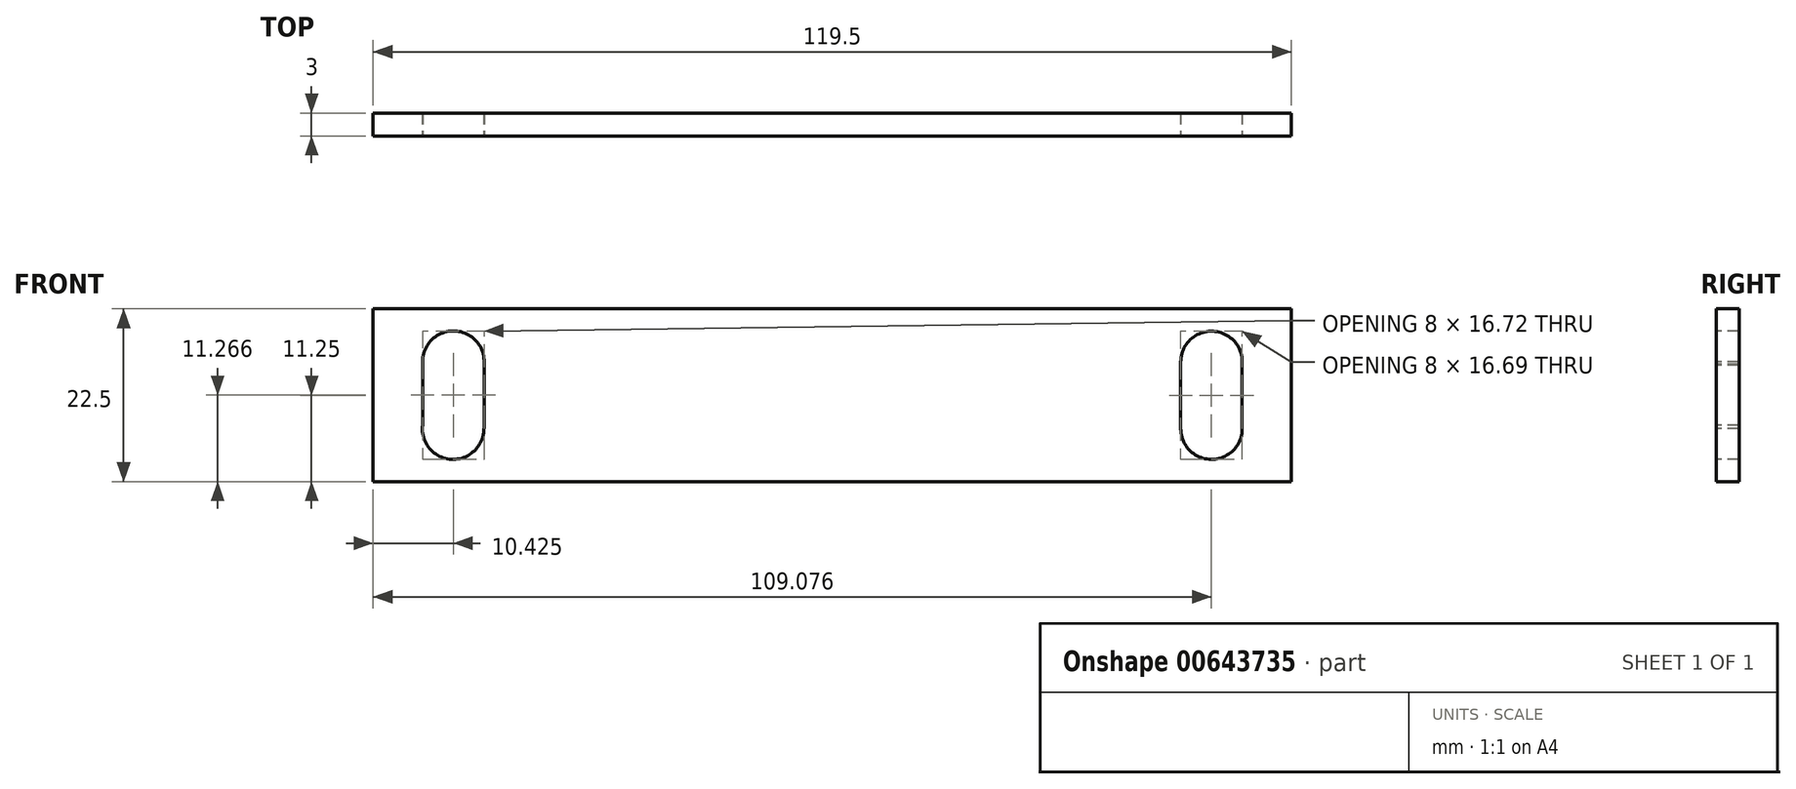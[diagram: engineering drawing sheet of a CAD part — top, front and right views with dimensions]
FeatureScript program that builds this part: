
annotation { "Feature Type Name" : "Feature", "Feature Type Description" : "" }
export const myFeature = defineFeature(function(context is Context, id is Id, definition is map)
    precondition{}
    {
        {
            var Q0;
            Q0=qCreatedBy(makeId("Front.planeOp"),FACE);
            var sketch = newSketch(context, id + "F0", { "sketchPlane" : qUnion([Q0])});
            skLineSegment(sketch, "E0.bottom", {"start": v(59.75, 11.25) * mm, "end": v(-59.75, 11.25) * mm});
            skLineSegment(sketch, "E0.top", {"start": v(59.75, -11.25) * mm, "end": v(-59.75, -11.25) * mm});
            skLineSegment(sketch, "E0.left", {"start": v(59.75, 11.25) * mm, "end": v(59.75, -11.25) * mm});
            skLineSegment(sketch, "E0.right", {"start": v(-59.75, 11.25) * mm, "end": v(-59.75, -11.25) * mm});
            skPoint(sketch, "E0.middle", {"position": v(0, 0) * mm});
            skSolve(sketch);
        }
        {
            var Q0;
            Q0=makeQuery(id+"F0.imprint","IMPRINT",FACE,{"disambiguationData":[TD([[makeQuery(id+"F0.imprint","IMPRINT",EDGE,{"derivedFrom":sQuery(id+"F0.wireOp",EDGE,"E0.bottom")}),1.0]])]});
            extrude(context, id + "F1", {"entities" : qUnion([Q0]), "depth" : 3 * mm, "offsetDistance" : 25 * mm});
        }
        {
            var Q0;
            Q0=makeQuery(id+"F1.opExtrude","CAP_FACE",FACE,{"disambiguationData":[OSD([sQuery(id+"F0.wireOp",EDGE,"E0.bottom"),sQuery(id+"F0.wireOp",EDGE,"E0.top"),sQuery(id+"F0.wireOp",EDGE,"E0.left"),sQuery(id+"F0.wireOp",EDGE,"E0.right")])],"isStart":false});
            var sketch = newSketch(context, id + "F2", { "sketchPlane" : qUnion([Q0])});
            skLineSegment(sketch, "E1", {"start": v(-59.75, -11.25) * mm, "end": v(-49.35, -11.25) * mm});
            skLineSegment(sketch, "E2", {"start": v(-49.35, -11.25) * mm, "end": v(-49.35, -4.35) * mm});
            skLineSegment(sketch, "E3", {"start": v(-59.75, 11.25) * mm, "end": v(-49.35, 11.25) * mm});
            skLineSegment(sketch, "E4", {"start": v(-49.3, 4.38) * mm, "end": v(-49.3, 11.28) * mm});
            skSolve(sketch);
        }
        {
            var Q0;
            Q0=sQuery(id+"F2.wireOp",VERTEX,"E4.start");
            var Q1;
            Q1=makeQuery(id+"F1.opExtrude","SWEPT_BODY",BODY,{"disambiguationData":[OSD([sQuery(id+"F0.wireOp",EDGE,"E0.bottom"),sQuery(id+"F0.wireOp",EDGE,"E0.top"),sQuery(id+"F0.wireOp",EDGE,"E0.left"),sQuery(id+"F0.wireOp",EDGE,"E0.right")])]});
            hole(context, id + "F3", {"style" : HoleStyle.SIMPLE, "endStyle" : HoleEndStyle.THROUGH, "holeDiameter" : 8 * mm, "majorDiameter" : 5 * mm, "isTappedThrough" : true, "tappedDepth" : 12 * mm, "tapClearance" : 3, "locations" : qUnion([Q0]), "scope" : qUnion([Q1])});
        }
        {
            var Q0;
            Q0=sQuery(id+"F2.wireOp",VERTEX,"E2.end");
            var Q1;
            Q1=makeQuery(id+"F1.opExtrude","SWEPT_BODY",BODY,{"disambiguationData":[OSD([sQuery(id+"F0.wireOp",EDGE,"E0.bottom"),sQuery(id+"F0.wireOp",EDGE,"E0.top"),sQuery(id+"F0.wireOp",EDGE,"E0.left"),sQuery(id+"F0.wireOp",EDGE,"E0.right")])]});
            hole(context, id + "F4", {"style" : HoleStyle.SIMPLE, "endStyle" : HoleEndStyle.THROUGH, "holeDiameter" : 8 * mm, "majorDiameter" : 5 * mm, "isTappedThrough" : true, "tappedDepth" : 12 * mm, "tapClearance" : 3, "locations" : qUnion([Q0]), "scope" : qUnion([Q1])});
        }
        {
            var Q0;
            {var subQ2=sQuery(id+"F2.wireOp",EDGE,"E1");Q0=makeQuery(id+"F2.imprint","IMPRINT",FACE,{"disambiguationData":[TD([[makeQuery(id+"F2.imprint","IMPRINT",EDGE,{"derivedFrom":subQ2}),-1.0]])]});}
            var sketch = newSketch(context, id + "F5", { "sketchPlane" : qUnion([Q0])});
            skLineSegment(sketch, "E5.bottom", {"start": v(-53.32, 4.37) * mm, "end": v(-45.32, 4.37) * mm});
            skLineSegment(sketch, "E5.top", {"start": v(-53.32, -4.33) * mm, "end": v(-45.32, -4.33) * mm});
            skLineSegment(sketch, "E5.left", {"start": v(-53.32, 4.37) * mm, "end": v(-53.32, -4.33) * mm});
            skLineSegment(sketch, "E5.right", {"start": v(-45.32, 4.37) * mm, "end": v(-45.32, -4.33) * mm});
            skSolve(sketch);
        }
        {
            var Q0;
            Q0 = qSketchRegion(id + "F5", true);
            extrude(context, id + "F6", {"entities" : qUnion([Q0]), "operationType" : NewBodyOperationType.REMOVE, "oppositeDirection" : true, "depth" : 3 * mm, "offsetDistance" : 25 * mm});
        }
        {
            var Q0;
            Q0=makeQuery(id+"F1.opExtrude","CAP_FACE",FACE,{"disambiguationData":[OSD([sQuery(id+"F0.wireOp",EDGE,"E0.bottom"),sQuery(id+"F0.wireOp",EDGE,"E0.top"),sQuery(id+"F0.wireOp",EDGE,"E0.left"),sQuery(id+"F0.wireOp",EDGE,"E0.right")])],"isStart":false});
            var sketch = newSketch(context, id + "F7", { "sketchPlane" : qUnion([Q0])});
            skLineSegment(sketch, "E6", {"start": v(59.75, -11.25) * mm, "end": v(49.35, -11.25) * mm});
            skLineSegment(sketch, "E7", {"start": v(59.75, 11.25) * mm, "end": v(49.35, 11.25) * mm});
            skLineSegment(sketch, "E8", {"start": v(49.35, 11.25) * mm, "end": v(49.35, 4.35) * mm});
            skLineSegment(sketch, "E9", {"start": v(49.35, -11.25) * mm, "end": v(49.35, -4.35) * mm});
            skSolve(sketch);
        }
        {
            var Q0;
            Q0=sQuery(id+"F7.wireOp",VERTEX,"E8.end");
            var Q1;
            Q1=makeQuery(id+"F1.opExtrude","SWEPT_BODY",BODY,{"disambiguationData":[OSD([sQuery(id+"F0.wireOp",EDGE,"E0.bottom"),sQuery(id+"F0.wireOp",EDGE,"E0.top"),sQuery(id+"F0.wireOp",EDGE,"E0.left"),sQuery(id+"F0.wireOp",EDGE,"E0.right")])]});
            hole(context, id + "F8", {"style" : HoleStyle.SIMPLE, "endStyle" : HoleEndStyle.THROUGH, "holeDiameter" : 8 * mm, "majorDiameter" : 5 * mm, "isTappedThrough" : true, "tappedDepth" : 12 * mm, "tapClearance" : 3, "locations" : qUnion([Q0]), "scope" : qUnion([Q1])});
        }
        {
            var Q0;
            Q0=sQuery(id+"F7.wireOp",VERTEX,"E9.end");
            var Q1;
            Q1=makeQuery(id+"F1.opExtrude","SWEPT_BODY",BODY,{"disambiguationData":[OSD([sQuery(id+"F0.wireOp",EDGE,"E0.bottom"),sQuery(id+"F0.wireOp",EDGE,"E0.top"),sQuery(id+"F0.wireOp",EDGE,"E0.left"),sQuery(id+"F0.wireOp",EDGE,"E0.right")])]});
            hole(context, id + "F9", {"style" : HoleStyle.SIMPLE, "endStyle" : HoleEndStyle.THROUGH, "holeDiameter" : 8 * mm, "majorDiameter" : 5 * mm, "isTappedThrough" : true, "tappedDepth" : 12 * mm, "tapClearance" : 3, "locations" : qUnion([Q0]), "scope" : qUnion([Q1])});
        }
        {
            var Q0;
            {var subQ1=sQuery(id+"F7.wireOp",EDGE,"E6");Q0=makeQuery(id+"F7.imprint","IMPRINT",FACE,{"disambiguationData":[TD([[makeQuery(id+"F7.imprint","IMPRINT",EDGE,{"derivedFrom":subQ1}),-1.0]])]});}
            var sketch = newSketch(context, id + "F10", { "sketchPlane" : qUnion([Q0])});
            skLineSegment(sketch, "E10.bottom", {"start": v(45.33, 4.34) * mm, "end": v(53.33, 4.34) * mm});
            skLineSegment(sketch, "E10.top", {"start": v(45.33, -4.36) * mm, "end": v(53.33, -4.36) * mm});
            skLineSegment(sketch, "E10.left", {"start": v(45.33, 4.34) * mm, "end": v(45.33, -4.36) * mm});
            skLineSegment(sketch, "E10.right", {"start": v(53.33, 4.34) * mm, "end": v(53.33, -4.36) * mm});
            skSolve(sketch);
        }
        {
            var Q0;
            Q0=makeQuery(id+"F10.imprint","IMPRINT",FACE,{"disambiguationData":[TD([[makeQuery(id+"F10.imprint","IMPRINT",EDGE,{"derivedFrom":sQuery(id+"F10.wireOp",EDGE,"E10.bottom")}),-1.0]])]});
            var sketch = newSketch(context, id + "F11", { "sketchPlane" : qUnion([Q0])});
            skSolve(sketch);
        }
        {
            var Q0;
            Q0=makeQuery(id+"F11.imprint","IMPRINT",FACE,{"disambiguationData":[TD([[makeQuery(id+"F11.imprint","IMPRINT",EDGE,{"derivedFrom":makeQuery(id+"F10.imprint","IMPRINT",EDGE,{"derivedFrom":sQuery(id+"F10.wireOp",EDGE,"E10.bottom")})}),-1.0]])]});
            var Q1;
            Q1=sQuery(id+"F10.wireOp",EDGE,"E10.bottom");
            var Q2;
            Q2=sQuery(id+"F10.wireOp",EDGE,"E10.left");
            var Q3;
            Q3=sQuery(id+"F10.wireOp",EDGE,"E10.right");
            var Q4;
            Q4=sQuery(id+"F10.wireOp",EDGE,"E10.top");
            extrude(context, id + "F12", {"entities" : qUnion([Q0]), "operationType" : NewBodyOperationType.REMOVE, "surfaceEntities" : qUnion([Q1, Q2, Q3, Q4]), "oppositeDirection" : true, "depth" : 3 * mm, "offsetDistance" : 25 * mm});
        }
    });
